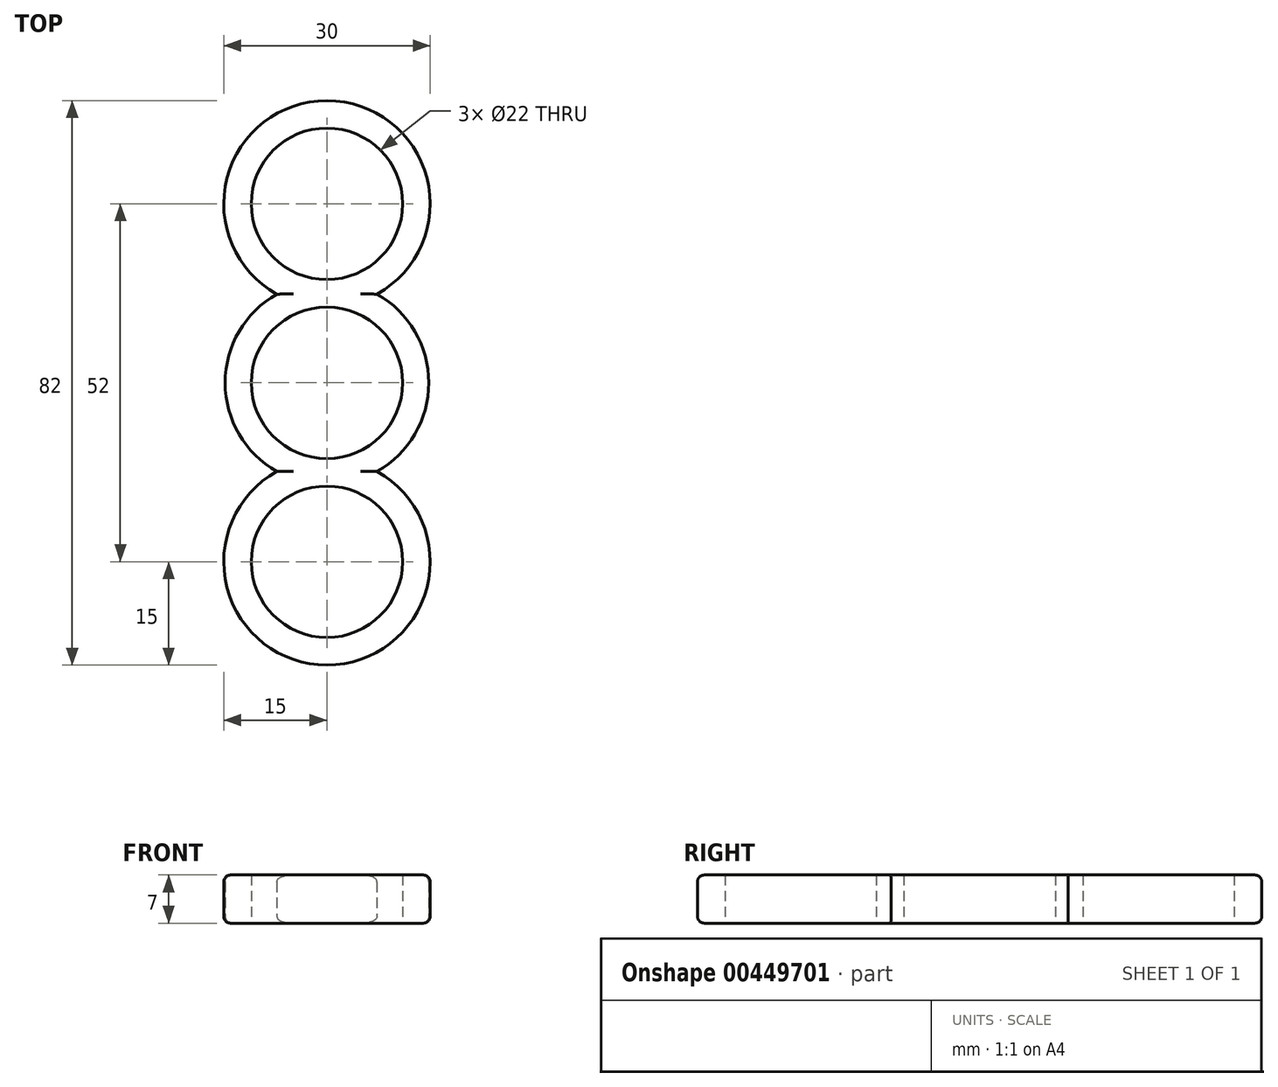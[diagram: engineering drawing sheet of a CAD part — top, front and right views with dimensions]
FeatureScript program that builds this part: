
annotation { "Feature Type Name" : "Feature", "Feature Type Description" : "" }
export const myFeature = defineFeature(function(context is Context, id is Id, definition is map)
    precondition{}
    {
        {
            var Q0;
            Q0=qCreatedBy(makeId("Top.planeOp"),FACE);
            var sketch = newSketch(context, id + "F0", { "sketchPlane" : qUnion([Q0])});
            skCircle(sketch, "E0", {"center": v(0, 0) * mm, "radius": 11 * mm});
            skArc(sketch, "E1", {"start": v(7.27, 12.88) * mm, "mid": v(0, 41) * mm, "end": v(-7.27, 12.88) * mm});
            skArc(sketch, "E2", {"start": v(-7.27, -12.88) * mm, "mid": v(0, -41) * mm, "end": v(7.27, -12.88) * mm});
            skCircle(sketch, "E3", {"center": v(0, 26) * mm, "radius": 11 * mm});
            skCircle(sketch, "E4", {"center": v(0, -26) * mm, "radius": 11 * mm});
            skArc(sketch, "E5", {"start": v(-7.27, 12.88) * mm, "mid": v(-14.8, 0) * mm, "end": v(-7.27, -12.88) * mm});
            skArc(sketch, "E6.trimOffspring", {"start": v(7.27, -12.88) * mm, "mid": v(14.8, 0) * mm, "end": v(7.27, 12.88) * mm});
            skSolve(sketch);
        }
        {
            var Q0;
            Q0=makeQuery(id+"F0.imprint","IMPRINT",FACE,{"disambiguationData":[TD([[makeQuery(id+"F0.imprint","IMPRINT",EDGE,{"derivedFrom":sQuery(id+"F0.wireOp",EDGE,"E0")}),-1.0]])]});
            extrude(context, id + "F1", {"entities" : qUnion([Q0]), "depth" : 7 * mm});
        }
        {
            var Q0;
            Q0=makeQuery(id+"F1.opExtrude","CAP_EDGE",EDGE,{"disambiguationData":[OSD([sQuery(id+"F0.wireOp",EDGE,"E2")])],"isStart":false});
            var Q1;
            Q1=makeQuery(id+"F1.opExtrude","CAP_EDGE",EDGE,{"disambiguationData":[OSD([sQuery(id+"F0.wireOp",EDGE,"E6.trimOffspring")])],"isStart":false});
            var Q2;
            Q2=makeQuery(id+"F1.opExtrude","CAP_EDGE",EDGE,{"disambiguationData":[OSD([sQuery(id+"F0.wireOp",EDGE,"E1")])],"isStart":false});
            var Q3;
            Q3=makeQuery(id+"F1.opExtrude","CAP_EDGE",EDGE,{"disambiguationData":[OSD([sQuery(id+"F0.wireOp",EDGE,"E5")])],"isStart":false});
            var Q4;
            Q4=makeQuery(id+"F1.opExtrude","CAP_EDGE",EDGE,{"disambiguationData":[OSD([sQuery(id+"F0.wireOp",EDGE,"E1")])],"isStart":true});
            var Q5;
            Q5=makeQuery(id+"F1.opExtrude","CAP_EDGE",EDGE,{"disambiguationData":[OSD([sQuery(id+"F0.wireOp",EDGE,"E6.trimOffspring")])],"isStart":true});
            var Q6;
            Q6=makeQuery(id+"F1.opExtrude","CAP_EDGE",EDGE,{"disambiguationData":[OSD([sQuery(id+"F0.wireOp",EDGE,"E2")])],"isStart":true});
            var Q7;
            Q7=makeQuery(id+"F1.opExtrude","CAP_EDGE",EDGE,{"disambiguationData":[OSD([sQuery(id+"F0.wireOp",EDGE,"E5")])],"isStart":true});
            fillet(context, id + "F2", {"entities" : qUnion([Q0, Q1, Q2, Q3, Q4, Q5, Q6, Q7]), "radius" : 1 * mm, "tangentPropagation" : true, "allowEdgeOverflow" : false});
        }
    });
